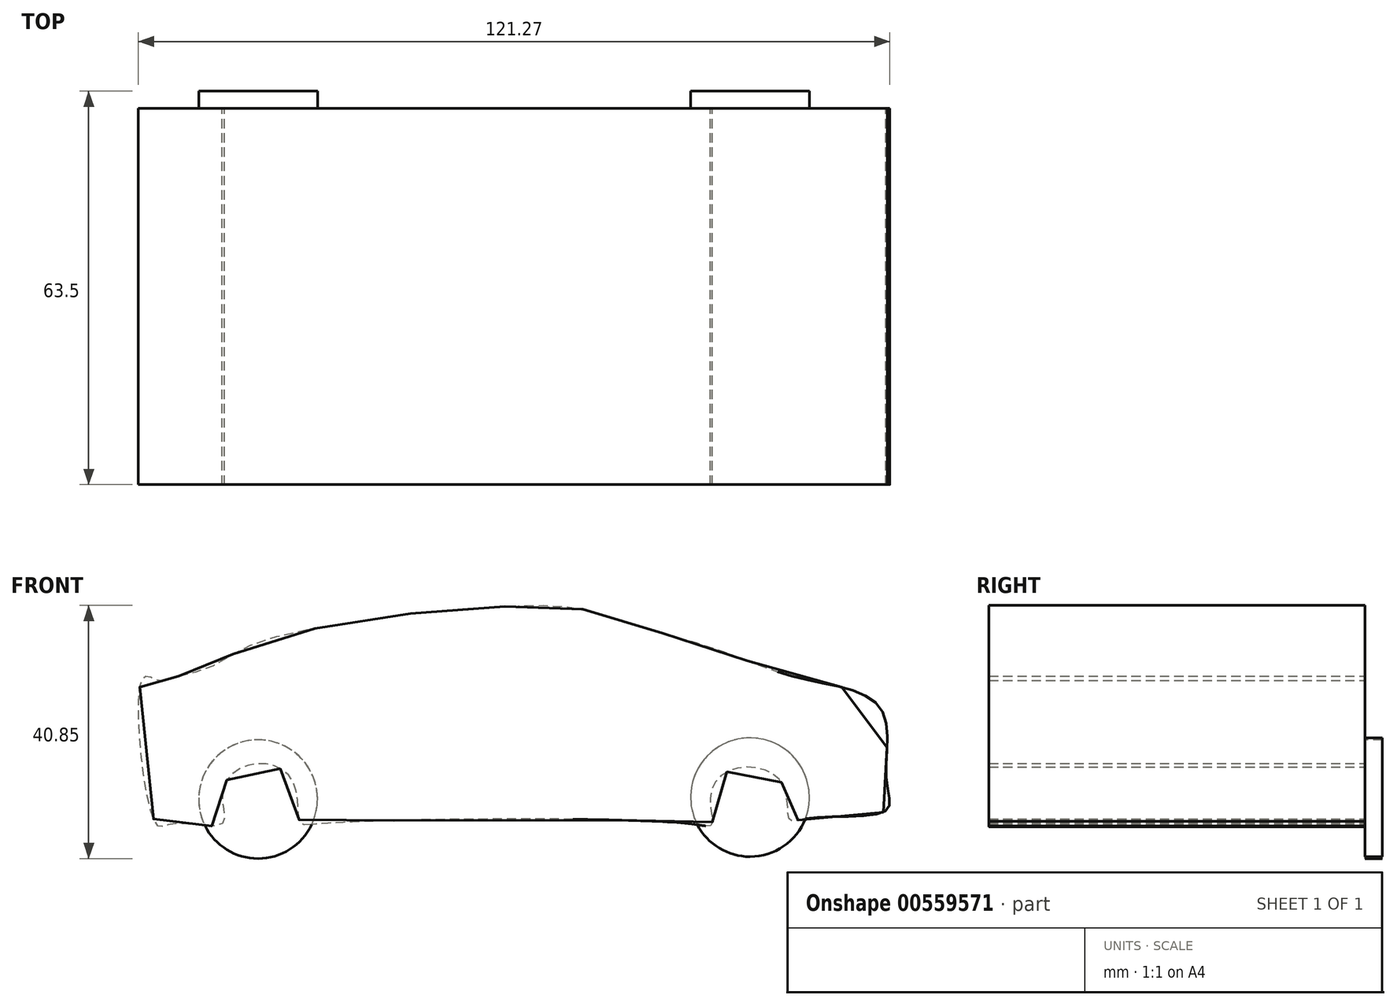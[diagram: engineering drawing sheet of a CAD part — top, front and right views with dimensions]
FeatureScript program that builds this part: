
annotation { "Feature Type Name" : "Feature", "Feature Type Description" : "" }
export const myFeature = defineFeature(function(context is Context, id is Id, definition is map)
    precondition{}
    {
        {
            var Q0;
            Q0=qCreatedBy(makeId("Front.planeOp"),FACE);
            var sketch = newSketch(context, id + "F0", { "sketchPlane" : qUnion([Q0])});
            skFitSpline(sketch, "E0", {"points": [v(-64.13, -14.05) * mm, v(-58.94, -12.52) * mm, v(-52.83, -9.16) * mm, v(-39.09, -5.8) * mm, v(-24.13, -3.66) * mm, v(-9.77, -2.75) * mm, v(0, -3.05) * mm, v(10.38, -6.1) * mm, v(22.9, -9.77) * mm, v(36.04, -14.35) * mm, v(49.17, -19.24) * mm, v(50.08, -30.84) * mm, v(50.08, -35.73) * mm, v(37.56, -36.95) * mm, v(34.5, -37.26) * mm, v(33.9, -32.98) * mm, v(30.84, -29.32) * mm, v(24.74, -29.32) * mm, v(21.68, -33.29) * mm, v(21.99, -37.87) * mm, v(18.32, -37.87) * mm, v(-41.23, -37.87) * mm, v(-44.59, -37.56) * mm, v(-45.2, -32.37) * mm, v(-48.25, -28.7) * mm, v(-53.75, -28.7) * mm, v(-57.1, -32.98) * mm, v(-57.1, -37.87) * mm, v(-65.05, -37.87) * mm, v(-67.8, -37.87) * mm, v(-69.93, -14.35) * mm, v(-67.49, -14.66) * mm, v(-64.13, -14.05) * mm]});
            skSolve(sketch);
        }
        {
            var Q0;
            Q0 = qSketchRegion(id + "F0", true);
            extrude(context, id + "F1", {"entities" : qUnion([Q0]), "depth" : 60.7 * mm, "offsetDistance" : 25.4 * mm});
        }
        {
            var Q0;
            Q0=qCreatedBy(makeId("Front.planeOp"),FACE);
            var sketch = newSketch(context, id + "F2", { "sketchPlane" : qUnion([Q0])});
            skCircle(sketch, "E1", {"center": v(-51.31, -33.9) * mm, "radius": 9.58 * mm});
            skCircle(sketch, "E2", {"center": v(28.09, -33.6) * mm, "radius": 9.59 * mm});
            skSolve(sketch);
        }
        {
            var Q0;
            Q0 = qSketchRegion(id + "F2", true);
            extrude(context, id + "F3", {"entities" : qUnion([Q0]), "operationType" : NewBodyOperationType.ADD, "oppositeDirection" : true, "depth" : 2.8 * mm, "offsetDistance" : 25.4 * mm});
        }
    });
